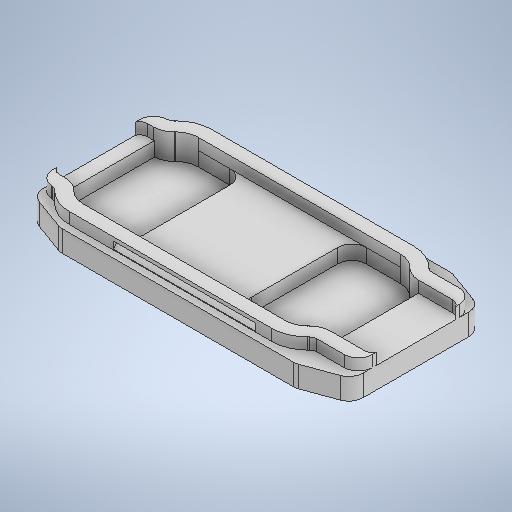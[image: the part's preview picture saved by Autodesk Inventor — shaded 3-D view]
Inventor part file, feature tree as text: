
AUTODESK INVENTOR PART (.ipt)
format: ipt  version: 2025.1 (Build 291241020, 241B)  size: 581,632 bytes
history: native  units: mm
features: extrude x5, sketch x5, projected_geometry x4
ambient origin geometry x8: Origin, YZ Plane, XZ Plane, XY Plane, X Axis, Y Axis, Z Axis, Center Point
bodies: Solid1 (feature_tree)
feature tree (14):
  extrude  "Extrusion1"  Depth=2.0mm
  extrude  "Extrusion2"  Depth=1.6mm TaperAngle=0.0deg
  extrude  "Extrusion3"  Depth=2.0mm
  extrude  "Extrusion4"  Depth=2.0mm
  extrude  "Extrusion5"  Depth=2.0mm TaperAngle=0.0deg
  sketch  "Sketch1"  dims[d0=2.0mm d1=2.0mm]
  sketch  "Sketch2"  dims[d2=2.0mm d3=1.6mm d4=0.0mm]
  sketch  "Sketch3"  dims[d6=2.0mm d7=2.0mm]
  projected_geometry  "Projected Loop3"
  sketch  "Sketch4"  dims[d8=2.0mm d9=2.0mm]
  projected_geometry  "Projected Loop4"
  sketch  "Sketch5"  dims[d10=2.0mm d11=2.0mm d12=0.0mm d13=1.0mm d14=0.0mm d15=2.0mm d16=2.0mm d19=2.0mm d20=4.268822mm d21=27.925268mm d22=27.925268mm d23=2.0mm d24=3.0mm d25=0.0mm d26=0.5mm d27=0.5mm d28=0.5mm d29=0.5mm d30=20.0mm d31=0.0mm d34=0.1mm]
  projected_geometry  "Projected Loop10"
  projected_geometry  "Projected Loop11"
